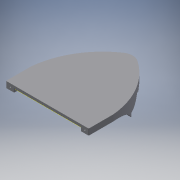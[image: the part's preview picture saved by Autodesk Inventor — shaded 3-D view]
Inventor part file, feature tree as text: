
AUTODESK INVENTOR PART (.ipt)
format: ipt  version: 2018 (Build 220112000, 112)  size: 597,504 bytes
history: native  units: mm
features: extrude x19, sketch x19, projected_geometry x18, other x12, reference x11, plane x5, fillet x4
ambient origin geometry x8: Origin, YZ Plane, XZ Plane, XY Plane, X Axis, Y Axis, Z Axis, Center Point
bodies: Solid1 (feature_tree)
feature tree (88):
  extrude  "Extrusion1"  Depth=40.0mm
  sketch  "Sketch3"  dims[d4=110.0mm d5=130.0mm]
  plane  "Work Plane1"
  extrude  "Extrusion2"  Depth=130.0mm
  extrude  "Extrusion3"  Depth=20.0mm
  extrude  "Extrusion4"  Depth=10.0mm TaperAngle=0.0deg
  extrude  "Extrusion5"  Depth=20.0mm
  extrude  "Extrusion6"  Depth=10.0mm
  other  "Work Point2"
  fillet  "Fillet1"  Radius=50.0mm
  plane  "Work Plane2"
  extrude  "Extrusion7"  Depth=35.0mm TaperAngle=0.0deg
  other  "Work Point3"
  plane  "Work Plane3"
  extrude  "Extrusion8"  Depth=160.0mm TaperAngle=0.0deg
  extrude  "Extrusion9"  Depth=160.0mm TaperAngle=0.0deg
  extrude  "Extrusion10"  Depth=1.0mm
  extrude  "Extrusion11"  Depth=20.0mm
  extrude  "Extrusion12"  Depth=20.0mm
  extrude  "Extrusion13"  Depth=20.0mm TaperAngle=0.0deg
  fillet  "Fillet2"  Radius=10.0mm
  extrude  "Extrusion14"  Depth=4.0mm
  fillet  "Fillet3"  Radius=20.0mm
  extrude  "Extrusion15"  Depth=20.0mm TaperAngle=0.0deg
  extrude  "Extrusion16"  Depth=20.0mm
  sketch  "Sketch20"  dims[d81=60.0mm d82=0.0mm d83=20.0mm]
  other  "Work Point4"
  other  "Work Point5"
  plane  "Work Plane4"
  plane  "Work Plane5"
  sketch  "Sketch21"  dims[d84=12.5mm d85=0.0mm d86=25.0mm]
  sketch  "Sketch22"  dims[d87=145.0mm d88=0.0mm d89=145.0mm d90=0.0mm]
  extrude  "Extrusion17"  Depth=25.0mm
  extrude  "Extrusion18"  Depth=145.0mm TaperAngle=0.0deg
  extrude  "Extrusion19"  Depth=1.0mm
  fillet  "Fillet4"  Radius=10.0mm
  sketch  "Sketch1"  dims[d2=40.0mm d3=40.0mm]
  reference  "Reference1"
  reference  "Reference2"
  other  "Work Point1"
  sketch  "Sketch5"  dims[d6=130.0mm d7=20.0mm]
  sketch  "Sketch8"  dims[d8=20.0mm d9=10.0mm d10=0.0mm]
  sketch  "Sketch9"  dims[d17=40.0mm d18=20.0mm]
  projected_geometry  "Projected Loop1"
  projected_geometry  "Projected Loop2"
  projected_geometry  "Projected Loop3"
  projected_geometry  "Projected Loop4"
  sketch  "Sketch10"  dims[d19=40.0mm d20=10.0mm d21=50.0mm]
  sketch  "Sketch11"  dims[d22=50.0mm d23=35.0mm d24=0.0mm]
  sketch  "Sketch12"  dims[d25=25.0mm d26=0.0mm d27=160.0mm d28=0.0mm]
  reference  "Reference3"
  reference  "Reference4"
  reference  "Reference5"
  reference  "Reference6"
  projected_geometry  "Projected Loop5"
  projected_geometry  "Projected Loop6"
  projected_geometry  "Projected Loop7"
  projected_geometry  "Projected Loop8"
  sketch  "Sketch13"  dims[d53=36.0mm d54=36.0mm d55=99.0mm d56=117.0mm d57=117.0mm d58=18.0mm d59=18.0mm d60=160.0mm d61=5.0mm d62=0.0mm d63=0.0mm]
  sketch  "Sketch14"  dims[d64=160.0mm d65=0.0mm d66=1.0mm]
  sketch  "Sketch15"  dims[d67=10.0mm d68=20.0mm]
  reference  "Reference7"
  reference  "Reference8"
  reference  "Reference9"
  reference  "Reference10"
  projected_geometry  "Projected Loop9"
  projected_geometry  "Projected Loop10"
  sketch  "Sketch16"  dims[d69=4.0mm d70=20.0mm]
  projected_geometry  "Projected Loop11"
  sketch  "Sketch17"  dims[d71=20.0mm d72=20.0mm d73=0.0mm d74=10.0mm]
  sketch  "Sketch18"  dims[d75=20.0mm d76=4.0mm d77=20.0mm]
  reference  "Reference11"
  sketch  "Sketch19"  dims[d78=20.0mm d79=20.0mm d80=0.0mm]
  projected_geometry  "Projected Loop12"
  sketch  "Sketch23"  dims[d91=40.0mm d92=0.0mm d93=1.0mm d94=10.0mm d95=10.0mm d96=0.0mm d97=1.0mm d98=2.75mm d99=8.0mm d100=0.0mm d101=10.0mm d102=0.0mm d103=5.0mm d104=5.0mm d105=6.0mm d106=5.2mm d107=6.0mm d108=5.2mm d109=20.0mm d110=0.0mm d111=20.0mm d112=0.0mm d113=20.0mm d114=0.0mm d115=2.0mm]
  projected_geometry  "Projected Loop13"
  projected_geometry  "Projected Loop14"
  projected_geometry  "Projected Loop15"
  projected_geometry  "Projected Loop16"
  projected_geometry  "Projected Loop17"
  projected_geometry  "Projected Loop18"
  other  "<userpath>\OneDrive\Documents\Inventor\TSA\2018\Animatronics\Tortoise\Head\HeadAssembly.iam"
  other  "HeadAssembly.iam"
  other  "HeadBase:1"
  other  "Rack:2"
  other  "Rack:1"
  other  "HeadBottom:2"
  other  "FlexHinge:1"
